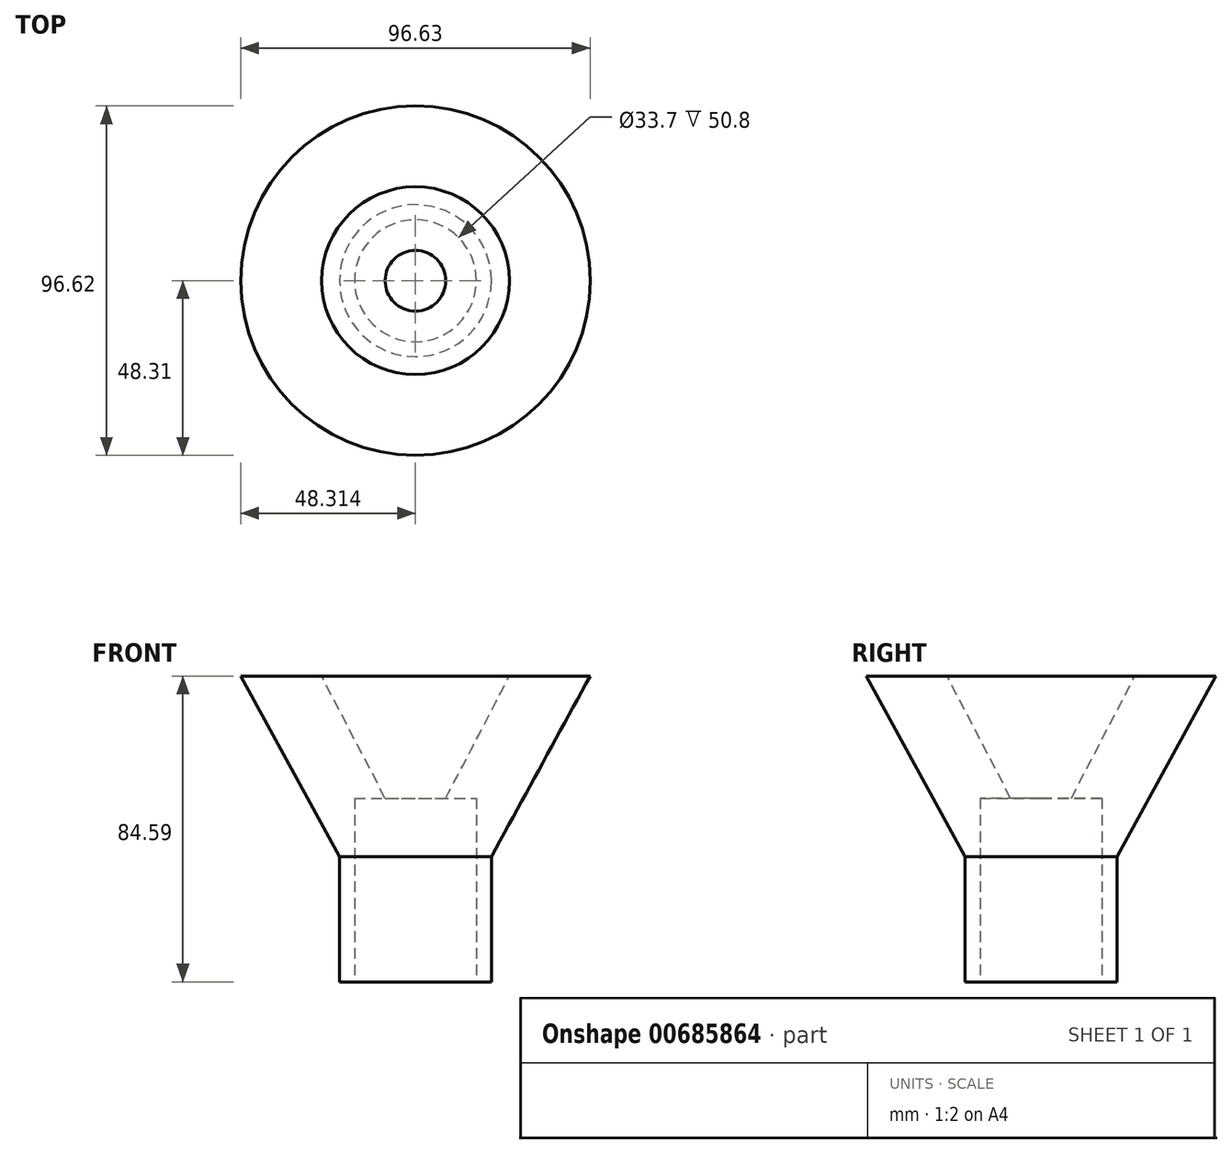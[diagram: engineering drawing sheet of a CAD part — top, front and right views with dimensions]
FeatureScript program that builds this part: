
annotation { "Feature Type Name" : "Feature", "Feature Type Description" : "" }
export const myFeature = defineFeature(function(context is Context, id is Id, definition is map)
    precondition{}
    {
        {
            var Q0;
            Q0=qCreatedBy(makeId("Front.planeOp"),FACE);
            var sketch = newSketch(context, id + "F0", { "sketchPlane" : qUnion([Q0])});
            skLineSegment(sketch, "E0", {"start": v(5.82, 0) * mm, "end": v(5.82, -34.66) * mm});
            skLineSegment(sketch, "E1", {"start": v(5.82, -34.66) * mm, "end": v(26.83, -34.66) * mm});
            skLineSegment(sketch, "E2", {"start": v(26.83, -34.66) * mm, "end": v(26.83, 0) * mm});
            skLineSegment(sketch, "E3", {"start": v(5.82, 0) * mm, "end": v(31.8, 49.93) * mm});
            skLineSegment(sketch, "E4", {"start": v(31.8, 49.93) * mm, "end": v(54.14, 49.93) * mm});
            skLineSegment(sketch, "E5", {"start": v(54.14, 49.93) * mm, "end": v(26.83, 0) * mm});
            skSolve(sketch);
        }
        {
            var Q0;
            Q0 = qSketchRegion(id + "F0", true);
            var Q1;
            Q1=sQuery(id+"F0.wireOp",EDGE,"E0");
            revolve(context, id + "F1", {"entities" : qUnion([Q0]), "axis" : qUnion([Q1]), "revolveType" : RevolveType.FULL});
        }
        {
            var Q0;
            Q0=makeQuery(id+"F1.opRevolve","SWEPT_FACE",FACE,{"disambiguationData":[OSD([sQuery(id+"F0.wireOp",EDGE,"E1")])]});
            var sketch = newSketch(context, id + "F2", { "sketchPlane" : qUnion([Q0])});
            skCircle(sketch, "E6", {"center": v(5.82, 0) * mm, "radius": 16.85 * mm});
            skSolve(sketch);
        }
        {
            var Q0;
            Q0=makeQuery(id+"F2.imprint","IMPRINT",FACE,{"disambiguationData":[TD([[makeQuery(id+"F2.imprint","IMPRINT",EDGE,{"derivedFrom":sQuery(id+"F2.wireOp",EDGE,"E6")}),1.0]])]});
            extrude(context, id + "F3", {"entities" : qUnion([Q0]), "operationType" : NewBodyOperationType.REMOVE, "oppositeDirection" : true, "depth" : 50.8 * mm, "offsetDistance" : 25.4 * mm});
        }
    });
